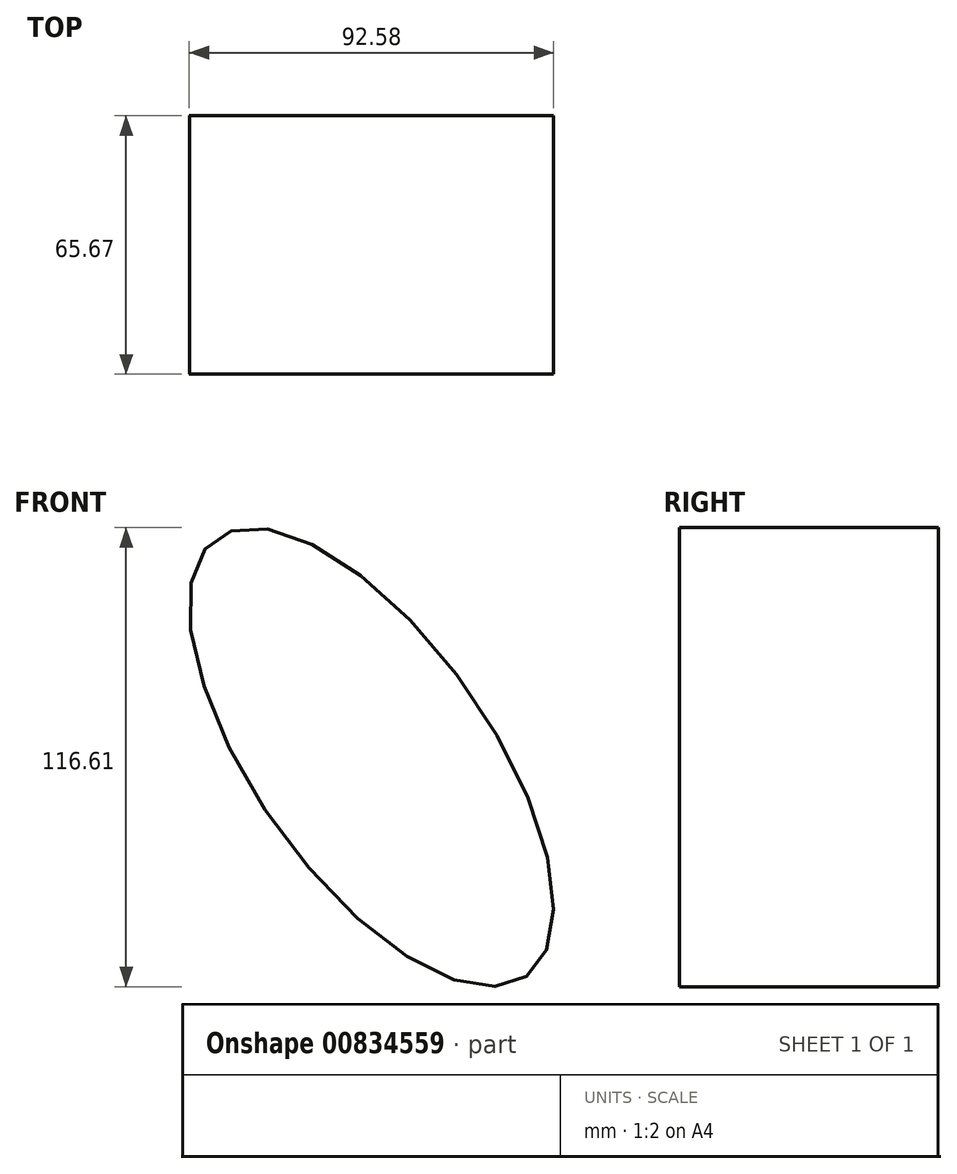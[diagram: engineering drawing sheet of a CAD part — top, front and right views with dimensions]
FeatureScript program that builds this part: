
annotation { "Feature Type Name" : "Feature", "Feature Type Description" : "" }
export const myFeature = defineFeature(function(context is Context, id is Id, definition is map)
    precondition{}
    {
        {
            var Q0;
            Q0=qCreatedBy(makeId("Front.planeOp"),FACE);
            var sketch = newSketch(context, id + "F0", { "sketchPlane" : qUnion([Q0])});
            skEllipse(sketch, "E0", {"center": v(15.82, 15.01) * mm, "majorRadius": 68.2 * mm, "minorRadius": 29.83 * mm, "majorAxis": v(0.58, -0.82)});
            skSolve(sketch);
        }
        {
            var Q0;
            Q0=makeQuery(id+"F0.imprint","IMPRINT",FACE,{"disambiguationData":[TD([[makeQuery(id+"F0.imprint","IMPRINT",EDGE,{"derivedFrom":sQuery(id+"F0.wireOp",EDGE,"E0")}),1.0]])]});
            extrude(context, id + "F1", {"entities" : qUnion([Q0]), "depth" : 65.67 * mm, "offsetDistance" : 25.4 * mm});
        }
    });
